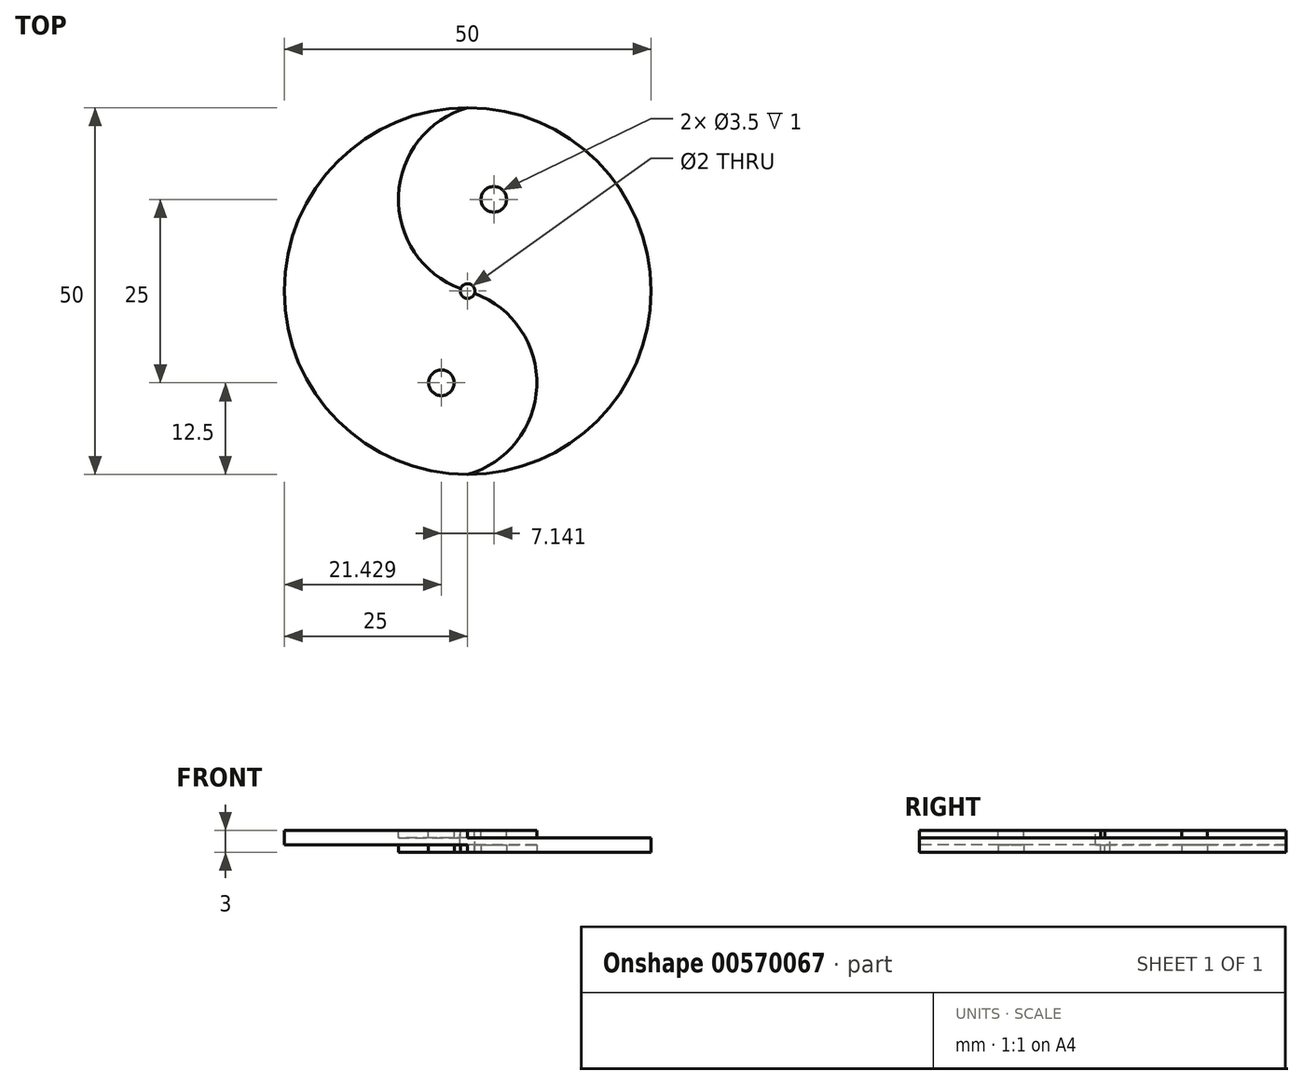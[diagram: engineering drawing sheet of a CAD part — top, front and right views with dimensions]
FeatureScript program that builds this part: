
annotation { "Feature Type Name" : "Feature", "Feature Type Description" : "" }
export const myFeature = defineFeature(function(context is Context, id is Id, definition is map)
    precondition{}
    {
        {
            var Q0;
            Q0=qCreatedBy(makeId("Top.planeOp"),FACE);
            var sketch = newSketch(context, id + "F0", { "sketchPlane" : qUnion([Q0])});
            skCircle(sketch, "E0", {"center": v(0, 0) * mm, "radius": 25 * mm});
            skSolve(sketch);
        }
        {
            var Q0;
            Q0=makeQuery(id+"F0.imprint","IMPRINT",FACE,{"disambiguationData":[TD([[makeQuery(id+"F0.imprint","IMPRINT",EDGE,{"derivedFrom":sQuery(id+"F0.wireOp",EDGE,"E0")}),1.0]])]});
            extrude(context, id + "F1", {"entities" : qUnion([Q0]), "depth" : 3 * mm, "offsetDistance" : 25 * mm});
        }
        {
            var Q0;
            Q0=makeQuery(id+"F1.opExtrude","CAP_FACE",FACE,{"disambiguationData":[OSD([sQuery(id+"F0.wireOp",EDGE,"E0")])],"isStart":false});
            var sketch = newSketch(context, id + "F2", { "sketchPlane" : qUnion([Q0])});
            skCircle(sketch, "E1", {"center": v(0, 0) * mm, "radius": 25 * mm});
            skArc(sketch, "E2", {"start": v(0, -25) * mm, "mid": v(9.43, -12.5) * mm, "end": v(0, 0) * mm});
            skArc(sketch, "E3", {"start": v(0, 25) * mm, "mid": v(-9.43, 12.5) * mm, "end": v(0, 0) * mm});
            skCircle(sketch, "E4", {"center": v(3.57, 12.5) * mm, "radius": 1.75 * mm});
            skCircle(sketch, "E5", {"center": v(-3.57, -12.5) * mm, "radius": 1.75 * mm});
            skSolve(sketch);
        }
        {
            var Q0;
            {var subQ0=sQuery(id+"F2.wireOp",EDGE,"E2");Q0=makeQuery(id+"F2.imprint","IMPRINT",FACE,{"disambiguationData":[TD([[makeQuery(id+"F2.imprint","IMPRINT",EDGE,{"derivedFrom":subQ0}),-1.0]])]});}
            var Q1;
            Q1=makeQuery(id+"F2.imprint","IMPRINT",FACE,{"disambiguationData":[TD([[makeQuery(id+"F2.imprint","IMPRINT",EDGE,{"derivedFrom":sQuery(id+"F2.wireOp",EDGE,"E5")}),1.0]])]});
            extrude(context, id + "F3", {"entities" : qUnion([Q0, Q1]), "operationType" : NewBodyOperationType.REMOVE, "oppositeDirection" : true, "depth" : 1 * mm, "offsetDistance" : 25 * mm});
        }
        {
            var Q0;
            Q0=makeQuery(id+"F1.opExtrude","CAP_FACE",FACE,{"disambiguationData":[OSD([sQuery(id+"F0.wireOp",EDGE,"E0")])],"isStart":true});
            var sketch = newSketch(context, id + "F4", { "sketchPlane" : qUnion([Q0])});
            skCircle(sketch, "E6", {"center": v(0, 0) * mm, "radius": 25 * mm});
            skArc(sketch, "E7", {"start": v(0, 0) * mm, "mid": v(9.43, 12.5) * mm, "end": v(0, 25) * mm});
            skArc(sketch, "E8", {"start": v(0, 0) * mm, "mid": v(-9.43, -12.5) * mm, "end": v(0, -25) * mm});
            skCircle(sketch, "E9", {"center": v(-3.57, 12.5) * mm, "radius": 1.75 * mm});
            skCircle(sketch, "E10", {"center": v(3.57, -12.5) * mm, "radius": 1.75 * mm});
            skSolve(sketch);
        }
        {
            var Q0;
            {var subQ0=sQuery(id+"F4.wireOp",EDGE,"E7");Q0=makeQuery(id+"F4.imprint","IMPRINT",FACE,{"disambiguationData":[TD([[makeQuery(id+"F4.imprint","IMPRINT",EDGE,{"derivedFrom":subQ0}),1.0]])]});}
            var Q1;
            Q1=makeQuery(id+"F4.imprint","IMPRINT",FACE,{"disambiguationData":[TD([[makeQuery(id+"F4.imprint","IMPRINT",EDGE,{"derivedFrom":sQuery(id+"F4.wireOp",EDGE,"E10")}),1.0]])]});
            extrude(context, id + "F5", {"entities" : qUnion([Q0, Q1]), "operationType" : NewBodyOperationType.REMOVE, "oppositeDirection" : true, "depth" : 1 * mm, "offsetDistance" : 25 * mm});
        }
        {
            var Q0;
            {var subQ0=sQuery(id+"F0.wireOp",EDGE,"E0");Q0=makeQuery(id+"F3.boolean.opBoolean","SPLIT",FACE,{"disambiguationData":[TD([makeQuery(id+"F1.opExtrude","SWEPT_FACE",FACE,{"disambiguationData":[OSD([subQ0])]})])],"derivedFrom":makeQuery(id+"F1.opExtrude","CAP_FACE",FACE,{"disambiguationData":[OSD([subQ0])],"isStart":false})});}
            var sketch = newSketch(context, id + "F6", { "sketchPlane" : qUnion([Q0])});
            skCircle(sketch, "E11", {"center": v(0, 0) * mm, "radius": 1 * mm});
            skSolve(sketch);
        }
        {
            var Q0;
            {var subQ0=sQuery(id+"F6.wireOp",EDGE,"E11");var subQ1=makeQuery(id+"F3.boolean.opBoolean","COPY",EDGE,{"derivedFrom":makeQuery(id+"F3.opExtrude","CAP_EDGE",EDGE,{"disambiguationData":[OSD([sQuery(id+"F2.wireOp",EDGE,"E2")])],"isStart":true})});var subQ2=makeQuery(id+"F6.imprint","INTERSECT",VERTEX,{"derivedFrom":[subQ1,subQ0]});Q0=makeQuery(id+"F6.imprint","IMPRINT",FACE,{"disambiguationData":[TD([[makeQuery(id+"F6.imprint","IMPRINT",EDGE,{"disambiguationData":[TD([[subQ2,-1.0]])],"derivedFrom":subQ0}),1.0]])]});}
            var Q1;
            {var subQ0=sQuery(id+"F6.wireOp",EDGE,"E11");var subQ1=makeQuery(id+"F3.boolean.opBoolean","COPY",EDGE,{"derivedFrom":makeQuery(id+"F3.opExtrude","CAP_EDGE",EDGE,{"disambiguationData":[OSD([sQuery(id+"F2.wireOp",EDGE,"E2")])],"isStart":true})});var subQ2=makeQuery(id+"F6.imprint","INTERSECT",VERTEX,{"derivedFrom":[subQ1,subQ0]});Q1=makeQuery(id+"F6.imprint","IMPRINT",FACE,{"disambiguationData":[TD([[makeQuery(id+"F6.imprint","IMPRINT",EDGE,{"disambiguationData":[TD([[subQ2,1.0]])],"derivedFrom":subQ0}),1.0]])]});}
            extrude(context, id + "F7", {"entities" : qUnion([Q0, Q1]), "operationType" : NewBodyOperationType.REMOVE, "oppositeDirection" : true, "depth" : 25 * mm, "offsetDistance" : 25 * mm});
        }
    });
